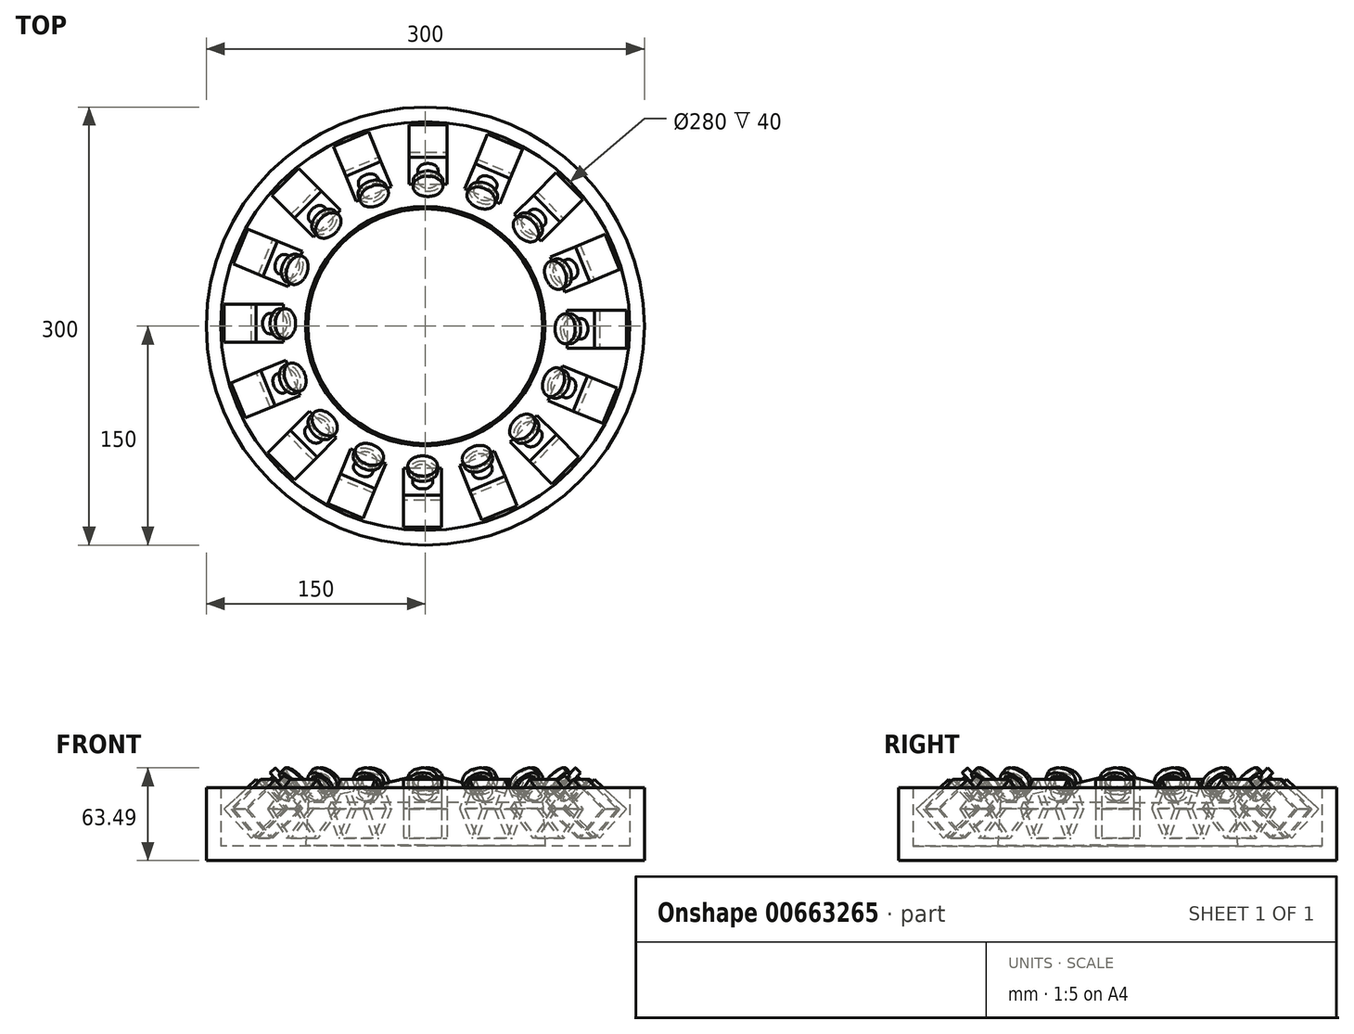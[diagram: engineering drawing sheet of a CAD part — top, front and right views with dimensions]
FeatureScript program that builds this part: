
annotation { "Feature Type Name" : "Feature", "Feature Type Description" : "" }
export const myFeature = defineFeature(function(context is Context, id is Id, definition is map)
    precondition{}
    {
        {
            var Q0;
            Q0=qCreatedBy(makeId("Top.planeOp"),FACE);
            var sketch = newSketch(context, id + "F0", { "sketchPlane" : qUnion([Q0])});
            skCircle(sketch, "E0", {"center": v(0, 0) * mm, "radius": 150 * mm});
            skSolve(sketch);
        }
        {
            var Q0;
            Q0=makeQuery(id+"F0.imprint","IMPRINT",FACE,{"disambiguationData":[TD([[makeQuery(id+"F0.imprint","IMPRINT",EDGE,{"derivedFrom":sQuery(id+"F0.wireOp",EDGE,"E0")}),1.0]])]});
            extrude(context, id + "F1", {"entities" : qUnion([Q0]), "depth" : 50 * mm, "offsetDistance" : 25.4 * mm});
        }
        {
            var Q0;
            Q0=makeQuery(id+"F1.opExtrude","CAP_FACE",FACE,{"disambiguationData":[OSD([sQuery(id+"F0.wireOp",EDGE,"E0")])],"isStart":false});
            shell(context, id + "F2", {"entities" : qUnion([Q0]), "thickness" : 10 * mm});
        }
        {
            var Q0;
            Q0=qCreatedBy(makeId("Front.planeOp"),FACE);
            var sketch = newSketch(context, id + "F3", { "sketchPlane" : qUnion([Q0])});
            skArc(sketch, "E1", {"start": v(0, 108.3) * mm, "mid": v(-77.25, 93.28) * mm, "end": v(-143.2, 50.34) * mm});
            skSolve(sketch);
        }
        {
            var Q0;
            Q0=qCreatedBy(makeId("Front.planeOp"),FACE);
            var sketch = newSketch(context, id + "F4", { "sketchPlane" : qUnion([Q0])});
            skLineSegment(sketch, "E2", {"start": v(0, 108.83) * mm, "end": v(0, 50.34) * mm, "construction": true});
            skSolve(sketch);
        }
        {
            var Q0;
            Q0=qCreatedBy(makeId("Front.planeOp"),FACE);
            var sketch = newSketch(context, id + "F5", { "sketchPlane" : qUnion([Q0])});
            skLineSegment(sketch, "E3", {"start": v(-117.35, 13.2) * mm, "end": v(-135.9, 33.13) * mm, "construction": true});
            skSolve(sketch);
        }
        {
            var Q0;
            Q0=sQuery(id+"F5.wireOp",EDGE,"E3");
            var Q1;
            Q1=qCreatedBy(makeId("Top.planeOp"),FACE);
            cPlane(context, id + "F6", {"entities" : qUnion([Q0, Q1]), "cplaneType" : CPlaneType.LINE_ANGLE, "offset" : 25.4 * mm, "angle" : 0 * degree, "width" : 152.4 * mm, "height" : 152.4 * mm});
        }
        {
            var Q0;
            Q0=qCreatedBy(id+"F6.planeOp",FACE);
            var sketch = newSketch(context, id + "F7", { "sketchPlane" : qUnion([Q0])});
            skLineSegment(sketch, "E4.bottom", {"start": v(10.99, 119.58) * mm, "end": v(-15.02, 119.58) * mm});
            skLineSegment(sketch, "E4.top", {"start": v(10.99, 92.34) * mm, "end": v(-15.02, 92.34) * mm});
            skLineSegment(sketch, "E4.left", {"start": v(10.99, 119.58) * mm, "end": v(10.99, 92.34) * mm});
            skLineSegment(sketch, "E4.right", {"start": v(-15.02, 119.58) * mm, "end": v(-15.02, 92.34) * mm});
            skSolve(sketch);
        }
        {
            var Q0;
            Q0 = qSketchRegion(id + "F7", true);
            extrude(context, id + "F8", {"entities" : qUnion([Q0]), "oppositeDirection" : true, "depth" : 30 * mm, "offsetDistance" : 25.4 * mm});
        }
        {
            var Q0;
            Q0=makeQuery(id+"F8.opExtrude","CAP_FACE",FACE,{"disambiguationData":[OSD([sQuery(id+"F7.wireOp",EDGE,"E4.bottom"),sQuery(id+"F7.wireOp",EDGE,"E4.top"),sQuery(id+"F7.wireOp",EDGE,"E4.left"),sQuery(id+"F7.wireOp",EDGE,"E4.right")])],"isStart":false});
            var sketch = newSketch(context, id + "F9", { "sketchPlane" : qUnion([Q0])});
            skCircle(sketch, "E5", {"center": v(1.8, 106.25) * mm, "radius": 6.94 * mm});
            skSolve(sketch);
        }
        {
            var Q0;
            Q0=makeQuery(id+"F9.imprint","IMPRINT",FACE,{"disambiguationData":[TD([[makeQuery(id+"F9.imprint","IMPRINT",EDGE,{"derivedFrom":sQuery(id+"F9.wireOp",EDGE,"E5")}),1.0]])]});
            extrude(context, id + "F10", {"entities" : qUnion([Q0]), "operationType" : NewBodyOperationType.ADD, "depth" : 10 * mm, "offsetDistance" : 25.4 * mm});
        }
        {
            var Q0;
            Q0=makeQuery(id+"F10.opExtrude","CAP_FACE",FACE,{"disambiguationData":[OSD([sQuery(id+"F9.wireOp",EDGE,"E5")])],"isStart":false});
            var sketch = newSketch(context, id + "F11", { "sketchPlane" : qUnion([Q0])});
            skCircle(sketch, "E6", {"center": v(1.8, 106.25) * mm, "radius": 10.2 * mm});
            skSolve(sketch);
        }
        {
            var Q0;
            Q0=makeQuery(id+"F11.imprint","IMPRINT",FACE,{"disambiguationData":[TD([[makeQuery(id+"F11.imprint","IMPRINT",EDGE,{"derivedFrom":sQuery(id+"F11.wireOp",EDGE,"E6")}),1.0]])]});
            var Q1;
            Q1=makeQuery(id+"F11.imprint","IMPRINT",FACE,{"disambiguationData":[TD([[makeQuery(id+"F11.imprint","IMPRINT",EDGE,{"derivedFrom":makeQuery(id+"F10.opExtrude","CAP_EDGE",EDGE,{"disambiguationData":[OSD([sQuery(id+"F9.wireOp",EDGE,"E5")])],"isStart":false})}),1.0]])]});
            extrude(context, id + "F12", {"entities" : qUnion([Q0, Q1]), "operationType" : NewBodyOperationType.ADD, "depth" : 5 * mm, "offsetDistance" : 25.4 * mm});
        }
        {
            var Q0;
            Q0=makeQuery(id+"F8.opExtrude","SWEPT_BODY",BODY,{"disambiguationData":[OSD([sQuery(id+"F7.wireOp",EDGE,"E4.bottom"),sQuery(id+"F7.wireOp",EDGE,"E4.top"),sQuery(id+"F7.wireOp",EDGE,"E4.left"),sQuery(id+"F7.wireOp",EDGE,"E4.right")])]});
            var Q1;
            Q1=sQuery(id+"F4.wireOp",EDGE,"E2");
            circularPattern(context, id + "F13", {"entities" : qUnion([Q0]), "axis" : qUnion([Q1]), "angle" : 360 * degree, "instanceCount" : 16, "equalSpace" : true});
        }
        {
            var Q0;
            Q0=qCreatedBy(makeId("Front.planeOp"),FACE);
            var sketch = newSketch(context, id + "F14", { "sketchPlane" : qUnion([Q0])});
            skLineSegment(sketch, "E7", {"start": v(-81.98, 10.18) * mm, "end": v(-80.36, 39.88) * mm});
            skLineSegment(sketch, "E8", {"start": v(0, 59.68) * mm, "end": v(-80.36, 39.88) * mm});
            skLineSegment(sketch, "E9", {"start": v(0, 59.68) * mm, "end": v(0, 10.4) * mm});
            skLineSegment(sketch, "E10", {"start": v(-81.98, 10.18) * mm, "end": v(0, 10.4) * mm});
            skSolve(sketch);
        }
        {
            var Q0;
            Q0=makeQuery(id+"F14.imprint","IMPRINT",FACE,{"disambiguationData":[TD([[makeQuery(id+"F14.imprint","IMPRINT",EDGE,{"derivedFrom":sQuery(id+"F14.wireOp",EDGE,"E7")}),-1.0]])]});
            var Q1;
            Q1=sQuery(id+"F14.wireOp",EDGE,"E7");
            var Q2;
            Q2=sQuery(id+"F14.wireOp",EDGE,"E8");
            var Q3;
            Q3=sQuery(id+"F14.wireOp",EDGE,"E10");
            var Q4;
            Q4=sQuery(id+"F14.wireOp",EDGE,"E9");
            revolve(context, id + "F15", {"entities" : qUnion([Q0]), "surfaceEntities" : qUnion([Q1, Q2, Q3]), "axis" : qUnion([Q4]), "revolveType" : RevolveType.FULL});
        }
        {
            var Q0;
            Q0=qCreatedBy(makeId("Top.planeOp"),FACE);
            cPlane(context, id + "F16", {"entities" : qUnion([Q0]), "cplaneType" : CPlaneType.OFFSET, "offset" : 60 * mm, "width" : 152.4 * mm, "height" : 152.4 * mm});
        }
        {
            var Q0;
            Q0=qCreatedBy(id+"F16.planeOp",FACE);
            var sketch = newSketch(context, id + "F17", { "sketchPlane" : qUnion([Q0])});
            skCircle(sketch, "E11.cCircle", {"center": v(-0.02, 0.78) * mm, "radius": 68.85 * mm, "construction": true});
            skLineSegment(sketch, "E11.0", {"start": v(-11.65, 68.63) * mm, "end": v(39.74, 56.98) * mm});
            skLineSegment(sketch, "E11.1", {"start": v(39.74, 56.98) * mm, "end": v(67.84, 12.4) * mm});
            skLineSegment(sketch, "E11.2", {"start": v(67.84, 12.4) * mm, "end": v(56.19, -38.98) * mm});
            skLineSegment(sketch, "E11.3", {"start": v(56.19, -38.98) * mm, "end": v(11.6, -67.08) * mm});
            skLineSegment(sketch, "E11.4", {"start": v(11.6, -67.08) * mm, "end": v(-39.78, -55.43) * mm});
            skLineSegment(sketch, "E11.5", {"start": v(-39.78, -55.43) * mm, "end": v(-67.88, -10.85) * mm});
            skLineSegment(sketch, "E11.6", {"start": v(-67.88, -10.85) * mm, "end": v(-56.23, 40.54) * mm});
            skLineSegment(sketch, "E11.7", {"start": v(-56.23, 40.54) * mm, "end": v(-11.65, 68.63) * mm});
            skSolve(sketch);
        }
        {
            var Q0;
            Q0=qCreatedBy(makeId("Top.planeOp"),FACE);
            cPlane(context, id + "F18", {"entities" : qUnion([Q0]), "cplaneType" : CPlaneType.OFFSET, "offset" : 160 * mm, "width" : 152.4 * mm, "height" : 152.4 * mm});
        }
        {
            var Q0;
            Q0=qCreatedBy(id+"F18.planeOp",FACE);
            var sketch = newSketch(context, id + "F19", { "sketchPlane" : qUnion([Q0])});
            skCircle(sketch, "E12.cCircle", {"center": v(1.41, 1.3) * mm, "radius": 87.71 * mm, "construction": true});
            skLineSegment(sketch, "E12.0", {"start": v(-13.6, 87.7) * mm, "end": v(51.9, 73.02) * mm});
            skLineSegment(sketch, "E12.1", {"start": v(51.9, 73.02) * mm, "end": v(87.83, 16.3) * mm});
            skLineSegment(sketch, "E12.2", {"start": v(87.83, 16.3) * mm, "end": v(73.13, -49.2) * mm});
            skLineSegment(sketch, "E12.3", {"start": v(73.13, -49.2) * mm, "end": v(16.43, -85.12) * mm});
            skLineSegment(sketch, "E12.4", {"start": v(16.43, -85.12) * mm, "end": v(-49.08, -70.43) * mm});
            skLineSegment(sketch, "E12.5", {"start": v(-49.08, -70.43) * mm, "end": v(-85, -13.72) * mm});
            skLineSegment(sketch, "E12.6", {"start": v(-85, -13.72) * mm, "end": v(-70.3, 51.78) * mm});
            skLineSegment(sketch, "E12.7", {"start": v(-70.3, 51.78) * mm, "end": v(-13.6, 87.7) * mm});
            skSolve(sketch);
        }
        {
            var Q0;
            Q0 = qConstructionFilter(qBodyType(qCreatedBy(id + "F17" ,EDGE), BodyType.WIRE), ConstructionObject.NO);
            var Q1;
            Q1 = qConstructionFilter(qBodyType(qCreatedBy(id + "F19" ,EDGE), BodyType.WIRE), ConstructionObject.NO);
            loft(context, id + "F20", {"bodyType" : ToolBodyType.SURFACE, "wireProfilesArray" : [{ "wireProfileEntities" : qUnion([Q0]) }, { "wireProfileEntities" : qUnion([Q1]) }]});
        }
        {
            var Q0;
            Q0=qCreatedBy(makeId("Front.planeOp"),FACE);
            var sketch = newSketch(context, id + "F21", { "sketchPlane" : qUnion([Q0])});
            skArc(sketch, "E13", {"start": v(0.31, 186.08) * mm, "mid": v(-101.2, 148.76) * mm, "end": v(-146.53, 50.55) * mm});
            skLineSegment(sketch, "E14", {"start": v(0.31, 60.8) * mm, "end": v(0.31, 186.08) * mm, "construction": true});
            skSolve(sketch);
        }
        {
            var Q0;
            Q0=sQuery(id+"F21.wireOp",EDGE,"E13");
            var Q1;
            Q1=sQuery(id+"F21.wireOp",EDGE,"E14");
            revolve(context, id + "F22", {"bodyType" : ToolBodyType.SURFACE, "surfaceEntities" : qUnion([Q0]), "axis" : qUnion([Q1]), "revolveType" : RevolveType.FULL});
        }
    });
